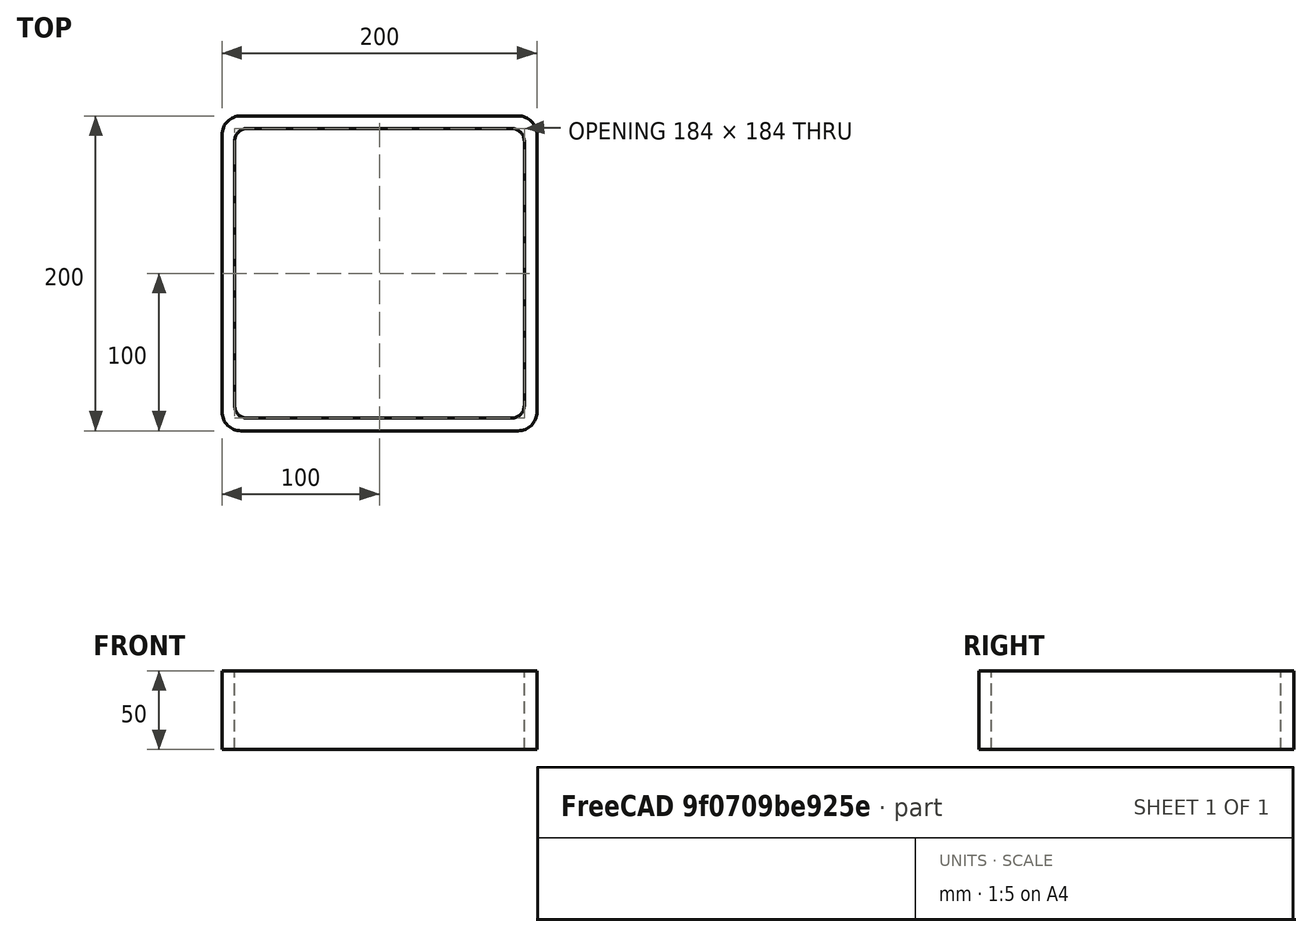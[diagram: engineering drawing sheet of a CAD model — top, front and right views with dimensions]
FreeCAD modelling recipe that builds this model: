
FCSTD DOCUMENT  (FreeCAD 0.15R4671 (Git))
Label: Square hollow section 200x200x8 EN10219 S235JRH
License: All rights reserved
LicenseURL: http://en.wikipedia.org/wiki/All_rights_reserved
objects: Sketcher::SketchObject×1, Part::Extrusion×1
note: 2 computed .brp shape members not serialized (recipe doc carries the construction recipe); baked Part::Feature solids carry a one-line shape summary decoded from their .brp

FEATURE [Sketcher::SketchObject] Sketch
  sketch-geometry (16):
    g0: LineSegment StartX=-84 StartY=92 StartZ=0 EndX=84 EndY=92 EndZ=0
    g1: LineSegment StartX=92 StartY=84 StartZ=0 EndX=92 EndY=-84 EndZ=0
    g2: LineSegment StartX=84 StartY=-92 StartZ=0 EndX=-84 EndY=-92 EndZ=0
    g3: LineSegment StartX=-92 StartY=-84 StartZ=0 EndX=-92 EndY=84 EndZ=0
    g4: LineSegment StartX=-88 StartY=100 StartZ=0 EndX=88 EndY=100 EndZ=0
    g5: LineSegment StartX=100 StartY=88 StartZ=0 EndX=100 EndY=-88 EndZ=0
    g6: LineSegment StartX=88 StartY=-100 StartZ=0 EndX=-88 EndY=-100 EndZ=0
    g7: LineSegment StartX=-100 StartY=-88 StartZ=0 EndX=-100 EndY=88 EndZ=0
    g8: ArcOfCircle CenterX=-84 CenterY=84 CenterZ=0 NormalX=0 NormalY=0 NormalZ=1 Radius=8 StartAngle=1.5708 EndAngle=3.14159
    g9: ArcOfCircle CenterX=84 CenterY=84 CenterZ=0 NormalX=0 NormalY=0 NormalZ=1 Radius=8 StartAngle=0 EndAngle=1.5708
    g10: ArcOfCircle CenterX=84 CenterY=-84 CenterZ=0 NormalX=0 NormalY=0 NormalZ=1 Radius=8 StartAngle=4.71239 EndAngle=6.28319
    g11: ArcOfCircle CenterX=-84 CenterY=-84 CenterZ=0 NormalX=0 NormalY=0 NormalZ=1 Radius=8 StartAngle=3.14159 EndAngle=4.71239
    g12: ArcOfCircle CenterX=88 CenterY=88 CenterZ=0 NormalX=0 NormalY=0 NormalZ=1 Radius=12 StartAngle=0 EndAngle=1.5708
    g13: ArcOfCircle CenterX=88 CenterY=-88 CenterZ=0 NormalX=0 NormalY=0 NormalZ=1 Radius=12 StartAngle=4.71239 EndAngle=6.28319
    g14: ArcOfCircle CenterX=-88 CenterY=-88 CenterZ=0 NormalX=0 NormalY=0 NormalZ=1 Radius=12 StartAngle=3.14159 EndAngle=4.71239
    g15: ArcOfCircle CenterX=-88 CenterY=88 CenterZ=0 NormalX=0 NormalY=0 NormalZ=1 Radius=12 StartAngle=1.5708 EndAngle=3.14159
  constraints (36):
    c: Horizontal(g2)
    c: Vertical(g3)
    c: Horizontal(g6)
    c: Vertical(g7)
    c: Tangent(g3,g8) = 1.5708
    c: Tangent(g0,g8) = 1.5708
    c: Tangent(g0,g9) = 1.5708
    c: Tangent(g1,g9) = 1.5708
    c: Tangent(g1,g10) = 1.5708
    c: Tangent(g2,g10) = 1.5708
    c: Tangent(g2,g11) = 1.5708
    c: Tangent(g3,g11) = 1.5708
    c: Tangent(g4,g12) = 1.5708
    c: Tangent(g5,g12) = 1.5708
    c: Tangent(g5,g13) = 1.5708
    c: Tangent(g6,g13) = 1.5708
    c: Tangent(g6,g14) = 1.5708
    c: Tangent(g7,g14) = 1.5708
    c: Tangent(g7,g15) = 1.5708
    c: Tangent(g4,g15) = 1.5708
    c: Equal(g9,g8)
    c: Equal(g9,g11)
    c: Equal(g9,g10)
    c: Equal(g12,g15)
    c: Equal(g12,g14)
    c: Equal(g12,g13)
    c: Symmetric(g4,g6,g-1)
    c: Symmetric(g7,g5,g-2)
    c: DistanceY(g4,g6) = -200
    c: DistanceX(g7,g5) = 200
    c: Symmetric(g3,g1,g-2)
    c: Symmetric(g0,g2,g-1)
    c: DistanceY(g0,g4) = 8
    c: DistanceX(g5,g1) = -8
    c: Radius(g9) = 8
    c: Radius(g12) = 12
FEATURE [Part::Extrusion] Extrude  label="Square hollow section 200x200x8 EN10219 S235JRH"
  Base = -> Sketch
  Dir = (0,0,50)
  Solid = true
